# Revit family: Doors_Garage_Overhead-Door-Corporation_RapidFlex-Flexible-Bottom-High-Speed-Door-990
name_source: partatom
category: Specialty Equipment
units: mm (PartAtom-declared; Revit-internal decimal feet)

## family parameters
Always vertical = Yes
Cut with Voids When Loaded = No
Host = Wall
OmniClass Number = 23.30.10.21.34
OmniClass Title = Industrial Doors
Part Type = Normal
Room Calculation Point = No
Round Connector Dimension = Use Diameter
Shared = No

## types (7) — shared parameters
Connector Description = Rapidflex Large Control Panel
Current = 20 A
Description = Our flexible bottom high speed interior fabric door, RapidFlex® 990, is ideal for high-traffic manufacturing, pharmaceutical, warehouse and distribution facilities.
Finish Material = Finish - Overhead Door - Yellow
Frequency = 60 Hz
Hood Material = Metal - Overhead Door - Black
Manufacturer = Overhead Door Corporation
Model = 990
Powder Coat (Note) = PowderGuard® Premium powder coat options are available in approximately 200 colors as well as custom matching to specification.
Power Factor = 1
Product Guid = b9145ded-ff11-484a-a30a-9068bf351ad7
Product Page URL = https://www.overheaddoor.com
Product data url = https://www.bimobject.com
URL = https://www.overheaddoor.com
Wall Closure = By host

## per-type parameters (varying)
| type | Apparent Load Phase 1 | Apparent Load Phase 2 | Apparent Load Phase 3 | External Transformer | Number of Poles | Voltage |
| 115 volts, one phase, 60 Hz (110-120V range) | 2300 VA | 0 VA | 0 VA | No | 1 | 115 V |
| 208 volts, one phase, 60 Hz (190-207V range) | 4160 VA | 0 VA | 0 VA | Yes | 1 | 208 V |
| 208 volts, three phase, 60 Hz (190-207 V range) | 2402 VA | 2402 VA | 2402 VA | Yes | 3 | 208 V |
| 230 volts, one phase, 60 Hz (208-245V range) | 4600 VA | 0 VA | 0 VA | No | 1 | 230 V |
| 230 volts, three phase, 60 Hz (208-245 V range) | 2656 VA | 2656 VA | 2656 VA | No | 3 | 230 V |
| 460 volts, three phase, 60 Hz (456-495 V range) | 5312 VA | 5312 VA | 5312 VA | No | 3 | 460 V |
| 575 volts, three phase, 60 Hz | 6640 VA | 6640 VA | 6640 VA | Yes | 3 | 575 V |

## geometry (parser evidence)
native form markers: Sweep x9
no freeform markers — native parametric forms only
